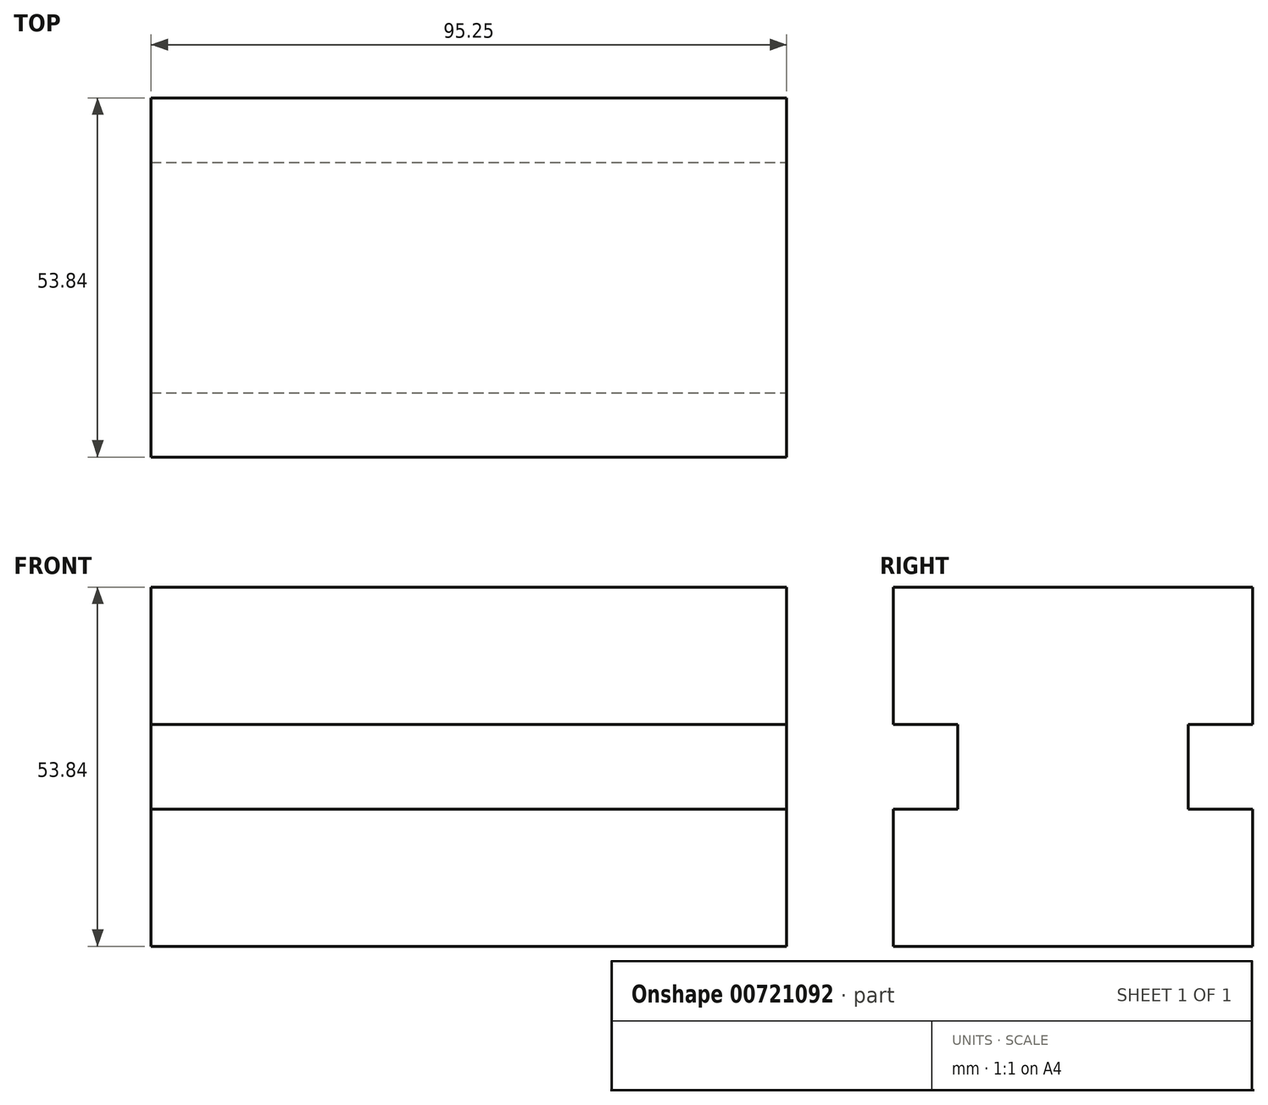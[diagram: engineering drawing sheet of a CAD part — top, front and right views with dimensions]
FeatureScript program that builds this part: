
annotation { "Feature Type Name" : "Feature", "Feature Type Description" : "" }
export const myFeature = defineFeature(function(context is Context, id is Id, definition is map)
    precondition{}
    {
        {
            var Q0;
            Q0=qCreatedBy(makeId("Right.planeOp"),FACE);
            var sketch = newSketch(context, id + "F0", { "sketchPlane" : qUnion([Q0])});
            skLineSegment(sketch, "E0.bottom", {"start": v(26.92, -26.92) * mm, "end": v(-26.92, -26.92) * mm});
            skLineSegment(sketch, "E0.top", {"start": v(26.92, 26.92) * mm, "end": v(-26.92, 26.92) * mm});
            skLineSegment(sketch, "E0.left", {"start": v(26.92, -26.92) * mm, "end": v(26.92, -6.35) * mm});
            skLineSegment(sketch, "E0.right", {"start": v(-26.92, -26.92) * mm, "end": v(-26.92, -6.35) * mm});
            skPoint(sketch, "E0.middle", {"position": v(0, 0) * mm});
            skLineSegment(sketch, "E1.bottom", {"start": v(-26.92, -6.35) * mm, "end": v(-17.27, -6.35) * mm});
            skLineSegment(sketch, "E1.top", {"start": v(-26.92, 6.35) * mm, "end": v(-17.27, 6.35) * mm});
            skLineSegment(sketch, "E1.right", {"start": v(-17.27, -6.35) * mm, "end": v(-17.27, 6.35) * mm});
            skLineSegment(sketch, "E2", {"start": v(0, 37.28) * mm, "end": v(0, -43.77) * mm, "construction": true});
            skPoint(sketch, "E2.startSnap0", {"position": v(0, 26.92) * mm});
            skLineSegment(sketch, "E3.MirrorCS", {"start": v(26.92, 6.35) * mm, "end": v(17.27, 6.35) * mm});
            skLineSegment(sketch, "E4.MirrorCS", {"start": v(26.92, -6.35) * mm, "end": v(17.27, -6.35) * mm});
            skLineSegment(sketch, "E5.MirrorCS", {"start": v(17.27, -6.35) * mm, "end": v(17.27, 6.35) * mm});
            skLineSegment(sketch, "E6.trimOffspring", {"start": v(-26.92, 6.35) * mm, "end": v(-26.92, 26.92) * mm});
            skLineSegment(sketch, "E7.trimOffspring", {"start": v(26.92, 6.35) * mm, "end": v(26.92, 26.92) * mm});
            skSolve(sketch);
        }
        {
            var Q0;
            Q0=makeQuery(id+"F0.imprint","IMPRINT",FACE,{"disambiguationData":[TD([[makeQuery(id+"F0.imprint","IMPRINT",EDGE,{"derivedFrom":sQuery(id+"F0.wireOp",EDGE,"E0.bottom")}),-1.0]])]});
            extrude(context, id + "F1", {"entities" : qUnion([Q0]), "oppositeDirection" : true, "depth" : 95.25 * mm, "offsetDistance" : 25.4 * mm});
        }
    });
